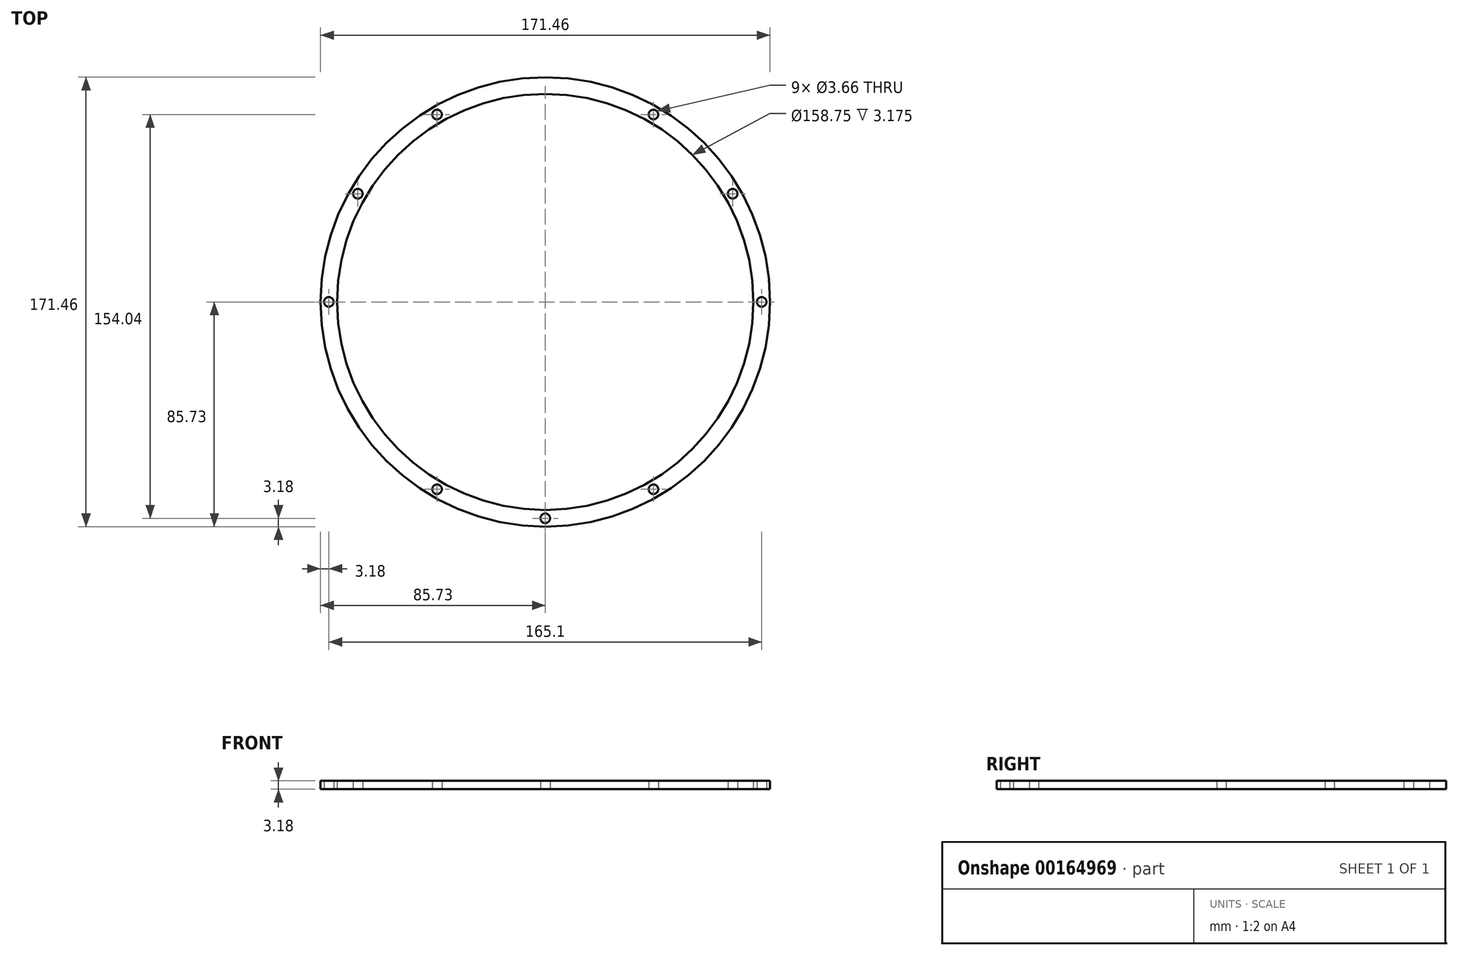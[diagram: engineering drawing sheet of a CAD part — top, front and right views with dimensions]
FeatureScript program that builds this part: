
annotation { "Feature Type Name" : "Feature", "Feature Type Description" : "" }
export const myFeature = defineFeature(function(context is Context, id is Id, definition is map)
    precondition{}
    {
        {
            var Q0;
            Q0=qCreatedBy(makeId("Top.planeOp"),FACE);
            var sketch = newSketch(context, id + "F0", { "sketchPlane" : qUnion([Q0])});
            skCircle(sketch, "E0", {"center": v(0, 0) * mm, "radius": 79.37 * mm});
            skCircle(sketch, "E1", {"center": v(0, 0) * mm, "radius": 85.72 * mm});
            skCircle(sketch, "E2.cCircle", {"center": v(0, 0) * mm, "radius": 71.5 * mm, "construction": true});
            skLineSegment(sketch, "E2.0", {"start": v(41.28, -71.5) * mm, "end": v(-41.27, -71.5) * mm, "construction": true});
            skLineSegment(sketch, "E2.1", {"start": v(-41.27, -71.5) * mm, "end": v(-82.55, 0) * mm, "construction": true});
            skLineSegment(sketch, "E2.2", {"start": v(-82.55, 0) * mm, "end": v(-41.28, 71.5) * mm, "construction": true});
            skLineSegment(sketch, "E2.3", {"start": v(-41.28, 71.5) * mm, "end": v(41.27, 71.5) * mm, "construction": true});
            skLineSegment(sketch, "E2.4", {"start": v(41.28, 71.5) * mm, "end": v(82.55, 0) * mm, "construction": true});
            skLineSegment(sketch, "E2.5", {"start": v(82.55, 0) * mm, "end": v(41.28, -71.5) * mm, "construction": true});
            skPoint(sketch, "E2.0.midPoint", {"position": v(0, -71.5) * mm});
            skCircle(sketch, "E3", {"center": v(41.28, -71.5) * mm, "radius": 3.18 * mm, "construction": true});
            skCircle(sketch, "E4", {"center": v(-41.27, -71.5) * mm, "radius": 1.83 * mm});
            skCircle(sketch, "E5", {"center": v(41.28, -71.5) * mm, "radius": 1.83 * mm});
            skCircle(sketch, "E6", {"center": v(-82.55, 0) * mm, "radius": 1.83 * mm});
            skCircle(sketch, "E7", {"center": v(82.55, 0) * mm, "radius": 1.83 * mm});
            skCircle(sketch, "E8", {"center": v(41.27, 71.5) * mm, "radius": 1.83 * mm});
            skCircle(sketch, "E9", {"center": v(-41.28, 71.5) * mm, "radius": 1.83 * mm});
            skCircle(sketch, "E10.cCircle", {"center": v(0, 0) * mm, "radius": 41.27 * mm, "construction": true});
            skLineSegment(sketch, "E10.0", {"start": v(-71.5, 41.27) * mm, "end": v(71.5, 41.28) * mm, "construction": true});
            skLineSegment(sketch, "E10.1", {"start": v(71.5, 41.28) * mm, "end": v(0, -82.55) * mm, "construction": true});
            skLineSegment(sketch, "E10.2", {"start": v(0, -82.55) * mm, "end": v(-71.5, 41.28) * mm, "construction": true});
            skPoint(sketch, "E10.0.midPoint", {"position": v(0, 41.27) * mm});
            skCircle(sketch, "E11", {"center": v(0, -82.55) * mm, "radius": 3.18 * mm, "construction": true});
            skCircle(sketch, "E12", {"center": v(0, -82.55) * mm, "radius": 1.83 * mm});
            skCircle(sketch, "E13", {"center": v(71.5, 41.28) * mm, "radius": 1.83 * mm});
            skCircle(sketch, "E14", {"center": v(-71.5, 41.27) * mm, "radius": 1.83 * mm});
            skSolve(sketch);
        }
        {
            var Q0;
            Q0=qSketchRegion(id+"F0",true);
            extrude(context, id + "F1", {"entities" : qUnion([Q0]), "depth" : 3.17 * mm});
        }
    });
